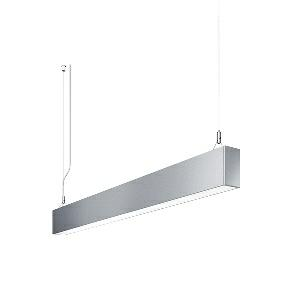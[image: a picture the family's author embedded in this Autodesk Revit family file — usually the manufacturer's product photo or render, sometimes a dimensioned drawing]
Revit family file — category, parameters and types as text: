
# Revit family: idoo_line_-_ilp_4000_840_d_00805676_edae
name_source: partatom
category: Lighting Fixtures
units: mm (PartAtom-declared; Revit-internal decimal feet)

## family parameters
Cut with Voids When Loaded = No
Host = Face
Light Source = No
Part Type = Normal
Room Calculation Point = No
Round Connector Dimension = Use Diameter
Shared = No

## types (1)
- IDOO.line - ILP 4000/840/D (1 x LED, 3950 lm, 4000K)
    Apparent Load = 29 VA
    Approval mark = CE
    CIE Flux Codes = 66 91 98 40 100
    Color Rendering = 80-89
    Color Temperature = 4000K
    Control Gear = Electronic ballast
    Default Elevation = 1800 mm
    Description = ILP 4000/840/D|Suspended luminaire|light source: LED|connected load: 220-240V, 50/60Hz|Power consumption: approx. 29 W|standby: approx. 0,15|luminous flux: 3950 lm|luminous efficacy: 136 lm/W|light distribution: Direct/indirect|direct ratio: approx. 40 %|colour temperature: Cold white, ca. 4000 K|color rendering index (CRI): >= 80|chromaticity tolerance:  3 SDCM|System of protection: IP 40|technology: Continuously dimmable|luminaire body|material: Sectional aluminium|colour: Silver|lamp cover: Acrylic (PMMA), Clear|mains lead: 2.00 m With free stranded wires|Fastening: Steel cable 0.3 - 0.7 m|glare control: Prism aperture|luminance(L65): <= 2700 cd/m|unified glare rating(4H 8H): <=  16|special features: DALI Load 1x, TouchDIM - dimming via standard switch, Flicker-free, Suitable as emergency lighting|
    Frequency = 50 Hz
    Height = 110 mm
    Lamp = 1 x LED
    Lamp Light Flux = 3950 lm
    Lamp count = 1
    Length = 1414 mm
    Luminous efficacy = 136 lm/W
    Manufacturer = Waldmann
    ModVariant = No
    Model = 00805676
    Mounting Place = Ceiling
    Mounting Type = Pendant
    Number of Poles = 1
    OnlyDefault = Yes
    Power Factor = 1
    Product Name = IDOO.line - ILP 4000/840/D
    Product group = Suspended luminaire
    ProductGroupID = 9
    Protection Class = Protection class I
    Protection Degree = IP 40
    RLX_Detail_Level = 1
    RLX_Emergency_Light_Flux = 0 lm
    RLX_Emergency_Type = 0
    RLX_Emergency_Type_DB = No
    RlxData = <blob elided: 21573 chars, md5=585d08d0>
    Socket = socket
    Standby Power = 0 W
    System Light Flux = 3950 lm
    System Power = 29 W
    Type Comments = Product without accessories
    Type Image = 113292000-00692525.jpg
    URL = http://relux.com
    VarID = ---
    Voltage = 230 V
    Voltage Range = 220-240 V
    Weight = 0.00 kg
    Width = 60 mm  [stored 0.19685 ft]

note: [stored X ft] marks values corroborated as IEEE doubles in the binary element streams (Revit-internal decimal feet)

## geometry (parser evidence)
native form markers: Blend x4, Sweep x12
no freeform markers — native parametric forms only
